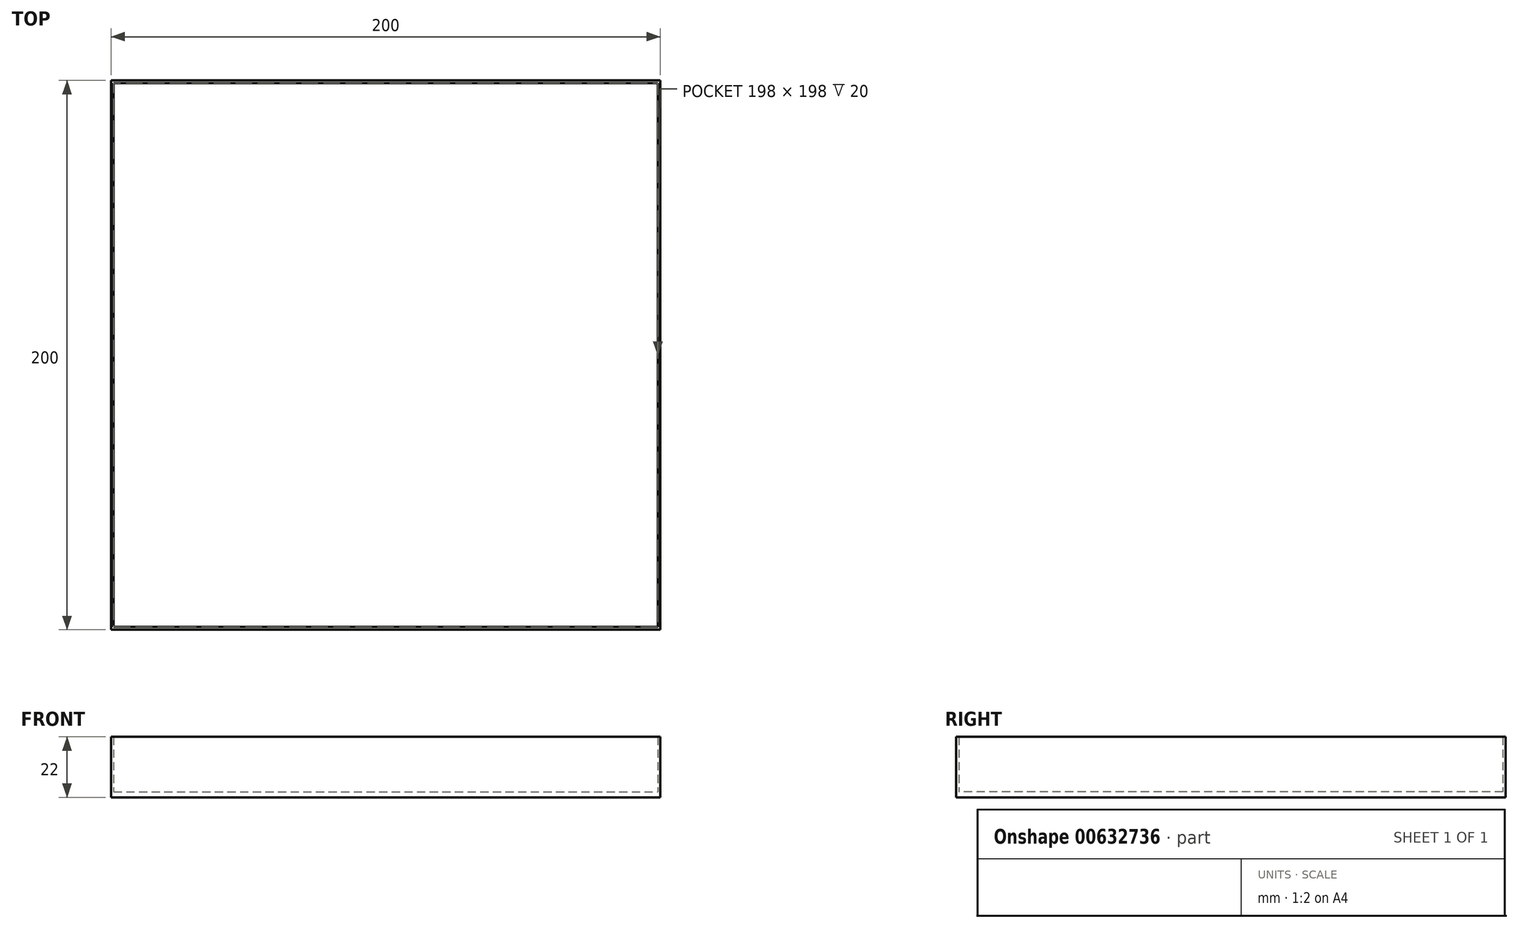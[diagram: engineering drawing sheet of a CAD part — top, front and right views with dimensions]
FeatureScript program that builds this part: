
annotation { "Feature Type Name" : "Feature", "Feature Type Description" : "" }
export const myFeature = defineFeature(function(context is Context, id is Id, definition is map)
    precondition{}
    {
        {
            var Q0;
            Q0=qCreatedBy(makeId("Top.planeOp"),FACE);
            var sketch = newSketch(context, id + "F0", { "sketchPlane" : qUnion([Q0])});
            skLineSegment(sketch, "E0.bottom", {"start": v(100, 100) * mm, "end": v(-100, 100) * mm});
            skLineSegment(sketch, "E0.top", {"start": v(100, -100) * mm, "end": v(-100, -100) * mm});
            skLineSegment(sketch, "E0.left", {"start": v(100, 100) * mm, "end": v(100, -100) * mm});
            skLineSegment(sketch, "E0.right", {"start": v(-100, 100) * mm, "end": v(-100, -100) * mm});
            skPoint(sketch, "E0.middle", {"position": v(0, 0) * mm});
            skLineSegment(sketch, "E1.bottom", {"start": v(-99, 99) * mm, "end": v(99, 99) * mm});
            skLineSegment(sketch, "E1.top", {"start": v(-99, -99) * mm, "end": v(99, -99) * mm});
            skLineSegment(sketch, "E1.left", {"start": v(-99, 99) * mm, "end": v(-99, -99) * mm});
            skLineSegment(sketch, "E1.right", {"start": v(99, 99) * mm, "end": v(99, -99) * mm});
            skSolve(sketch);
        }
        {
            var Q0;
            Q0 = qSketchRegion(id + "F0", true);
            extrude(context, id + "F1", {"entities" : qUnion([Q0]), "depth" : 20 * mm, "offsetDistance" : 25 * mm});
        }
        {
            var Q0;
            Q0=qCreatedBy(makeId("Top.planeOp"),FACE);
            var sketch = newSketch(context, id + "F2", { "sketchPlane" : qUnion([Q0])});
            skLineSegment(sketch, "E2.bottom", {"start": v(-100, 100) * mm, "end": v(100, 100) * mm});
            skLineSegment(sketch, "E2.top", {"start": v(-100, -100) * mm, "end": v(100, -100) * mm});
            skLineSegment(sketch, "E2.left", {"start": v(-100, 100) * mm, "end": v(-100, -100) * mm});
            skLineSegment(sketch, "E2.right", {"start": v(100, 100) * mm, "end": v(100, -100) * mm});
            skPoint(sketch, "E2.middle", {"position": v(0, 0) * mm});
            skSolve(sketch);
        }
        {
            var Q0;
            Q0=makeQuery(id+"F2.imprint","IMPRINT",FACE,{"disambiguationData":[TD([[makeQuery(id+"F2.imprint","IMPRINT",EDGE,{"derivedFrom":sQuery(id+"F2.wireOp",EDGE,"E2.bottom")}),-1.0]])]});
            extrude(context, id + "F3", {"entities" : qUnion([Q0]), "operationType" : NewBodyOperationType.ADD, "oppositeDirection" : true, "depth" : 2 * mm, "offsetDistance" : 25 * mm});
        }
    });
